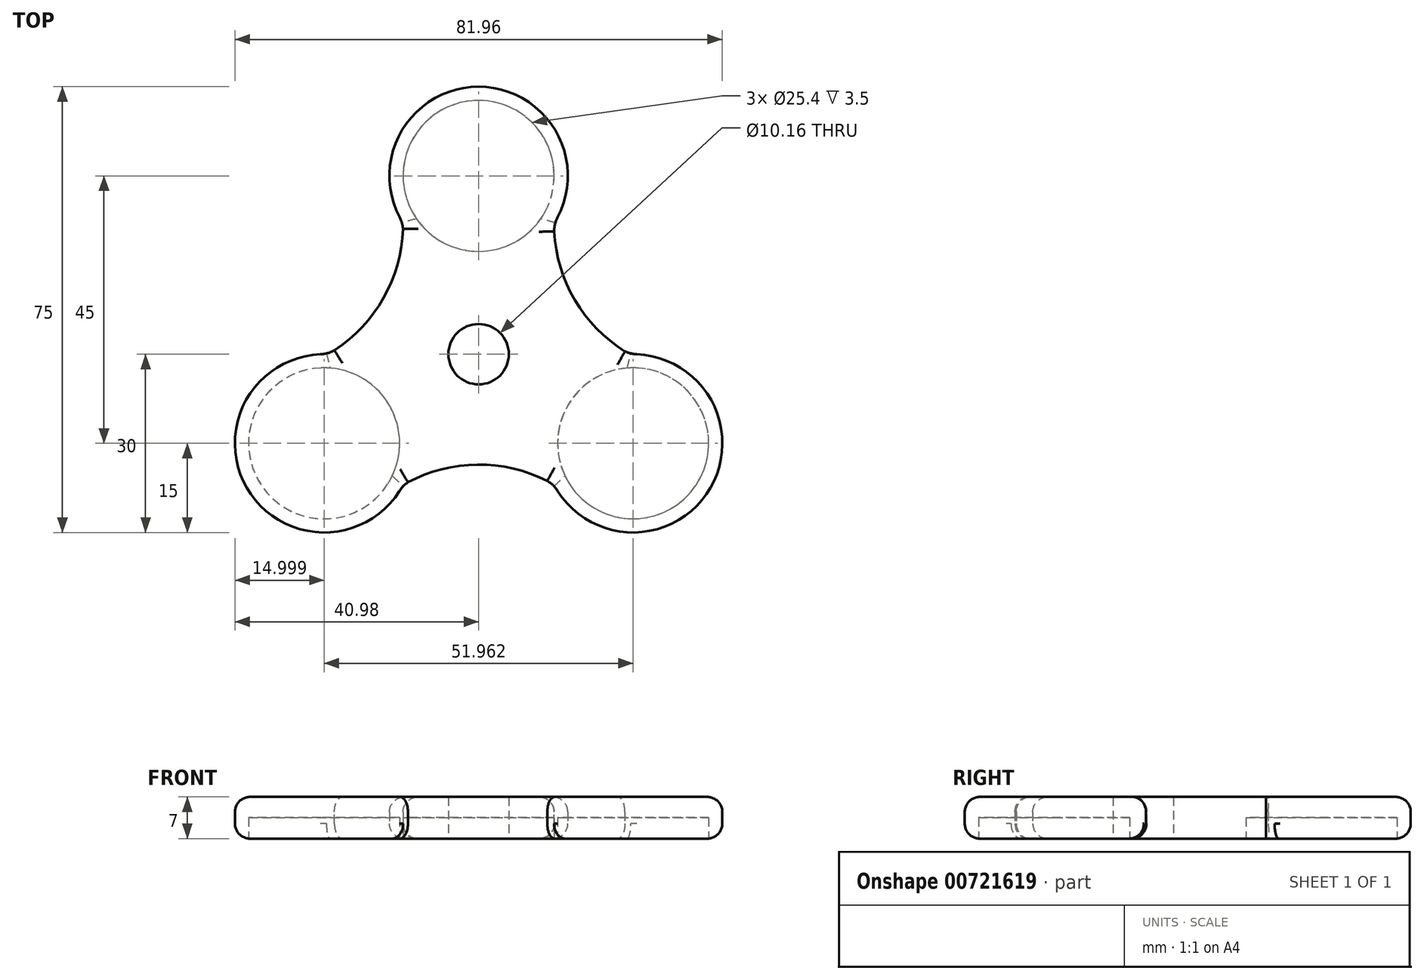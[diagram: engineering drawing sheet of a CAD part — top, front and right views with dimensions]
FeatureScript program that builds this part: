
annotation { "Feature Type Name" : "Feature", "Feature Type Description" : "" }
export const myFeature = defineFeature(function(context is Context, id is Id, definition is map)
    precondition{}
    {
        {
            var Q0;
            Q0=qCreatedBy(makeId("Top.planeOp"),FACE);
            var sketch = newSketch(context, id + "F0", { "sketchPlane" : qUnion([Q0])});
            skCircle(sketch, "E0", {"center": v(0, 0) * mm, "radius": 15 * mm});
            skCircle(sketch, "E1", {"center": v(0, 30) * mm, "radius": 15 * mm});
            skCircle(sketch, "E2", {"center": v(0, 30) * mm, "radius": 12.7 * mm});
            skCircle(sketch, "E3", {"center": v(0, 0) * mm, "radius": 5.08 * mm});
            skLineSegment(sketch, "E4", {"start": v(0, 30) * mm, "end": v(0, 15) * mm, "construction": true});
            skLineSegment(sketch, "E5", {"start": v(0, 0) * mm, "end": v(0, 15) * mm, "construction": true});
            skLineSegment(sketch, "E6", {"start": v(0, 0) * mm, "end": v(0, -15) * mm});
            skLineSegment(sketch, "E7", {"start": v(0, 0) * mm, "end": v(15, 0) * mm});
            skLineSegment(sketch, "E8", {"start": v(0, 0) * mm, "end": v(-15, 0) * mm});
            skLineSegment(sketch, "E9", {"start": v(0, 30) * mm, "end": v(-20.54, 30) * mm, "construction": true});
            skLineSegment(sketch, "E10", {"start": v(-25.98, -15) * mm, "end": v(-25.98, 30.15) * mm, "construction": true});
            skPoint(sketch, "E11", {"position": v(-25.98, 0) * mm});
            skPoint(sketch, "E12", {"position": v(-15, 30) * mm});
            skLineSegment(sketch, "E13.0", {"start": v(12.7, 30) * mm, "end": v(12.7, 15) * mm});
            skLineSegment(sketch, "E13.1", {"start": v(12.7, 0) * mm, "end": v(12.7, 15) * mm});
            skLineSegment(sketch, "E14.0", {"start": v(-12.7, 30) * mm, "end": v(-12.7, 15) * mm});
            skLineSegment(sketch, "E14.1", {"start": v(-12.7, 0) * mm, "end": v(-12.7, 15) * mm});
            skPoint(sketch, "E15.1.0", {"position": v(-18.48, -28) * mm});
            skLineSegment(sketch, "E15.1.1", {"start": v(-19.63, -26) * mm, "end": v(-6.64, -18.5) * mm});
            skLineSegment(sketch, "E15.1.2", {"start": v(-32.33, -4) * mm, "end": v(-19.34, 3.5) * mm});
            skLineSegment(sketch, "E15.1.3", {"start": v(-25.98, -15) * mm, "end": v(-15.71, -32.78) * mm, "construction": true});
            skLineSegment(sketch, "E15.1.4", {"start": v(-25.98, -15) * mm, "end": v(-13, -7.5) * mm, "construction": true});
            skCircle(sketch, "E15.1.5", {"center": v(-25.98, -15) * mm, "radius": 12.7 * mm});
            skCircle(sketch, "E15.1.6", {"center": v(-25.98, -15) * mm, "radius": 15 * mm});
            skLineSegment(sketch, "E15.1.7", {"start": v(6.35, -11) * mm, "end": v(-6.64, -18.5) * mm});
            skLineSegment(sketch, "E15.1.8", {"start": v(-6.35, 11) * mm, "end": v(-19.34, 3.5) * mm});
            skLineSegment(sketch, "E15.1.9", {"start": v(0, 0) * mm, "end": v(-13, -7.5) * mm, "construction": true});
            skPoint(sketch, "E15.2.0", {"position": v(33.48, -2) * mm});
            skLineSegment(sketch, "E15.2.1", {"start": v(32.33, -4) * mm, "end": v(19.34, 3.5) * mm});
            skLineSegment(sketch, "E15.2.2", {"start": v(19.63, -26) * mm, "end": v(6.64, -18.5) * mm});
            skLineSegment(sketch, "E15.2.3", {"start": v(25.98, -15) * mm, "end": v(36.25, 2.78) * mm, "construction": true});
            skLineSegment(sketch, "E15.2.4", {"start": v(25.98, -15) * mm, "end": v(13, -7.5) * mm, "construction": true});
            skCircle(sketch, "E15.2.5", {"center": v(25.98, -15) * mm, "radius": 12.7 * mm});
            skCircle(sketch, "E15.2.6", {"center": v(25.98, -15) * mm, "radius": 15 * mm});
            skLineSegment(sketch, "E15.2.7", {"start": v(6.35, 11) * mm, "end": v(19.34, 3.5) * mm});
            skLineSegment(sketch, "E15.2.8", {"start": v(-6.35, -11) * mm, "end": v(6.64, -18.5) * mm});
            skLineSegment(sketch, "E15.2.9", {"start": v(0, 0) * mm, "end": v(13, -7.5) * mm, "construction": true});
            skSolve(sketch);
        }
        {
            var Q0;
            {var subQ0=sQuery(id+"F0.wireOp",EDGE,"E14.0");var subQ1=sQuery(id+"F0.wireOp",EDGE,"E1");var subQ2=makeQuery(id+"F0.imprint","INTERSECT",VERTEX,{"derivedFrom":[subQ1,subQ0]});Q0=makeQuery(id+"F0.imprint","IMPRINT",FACE,{"disambiguationData":[TD([[makeQuery(id+"F0.imprint","IMPRINT",EDGE,{"disambiguationData":[TD([[subQ2,1.0]])],"derivedFrom":subQ1}),1.0]])]});}
            var Q1;
            {var subQ0=sQuery(id+"F0.wireOp",EDGE,"E13.1");var subQ1=sQuery(id+"F0.wireOp",EDGE,"E0");var subQ2=makeQuery(id+"F0.imprint","INTERSECT",VERTEX,{"derivedFrom":[subQ1,subQ0]});Q1=makeQuery(id+"F0.imprint","IMPRINT",FACE,{"disambiguationData":[TD([[makeQuery(id+"F0.imprint","IMPRINT",EDGE,{"disambiguationData":[TD([[subQ2,-1.0]])],"derivedFrom":subQ1}),-1.0]])]});}
            var Q2;
            {var subQ0=sQuery(id+"F0.wireOp",EDGE,"E14.1");var subQ1=sQuery(id+"F0.wireOp",EDGE,"E0");var subQ2=makeQuery(id+"F0.imprint","INTERSECT",VERTEX,{"derivedFrom":[subQ1,subQ0]});Q2=makeQuery(id+"F0.imprint","IMPRINT",FACE,{"disambiguationData":[TD([[makeQuery(id+"F0.imprint","IMPRINT",EDGE,{"disambiguationData":[TD([[subQ2,1.0]])],"derivedFrom":subQ1}),-1.0]])]});}
            var Q3;
            {var subQ1=sQuery(id+"F0.wireOp",EDGE,"E1");var subQ5=sQuery(id+"F0.wireOp",EDGE,"E14.0");var subQ8=makeQuery(id+"F0.imprint","INTERSECT",VERTEX,{"derivedFrom":[subQ1,subQ5]});Q3=makeQuery(id+"F0.imprint","IMPRINT",FACE,{"disambiguationData":[TD([[makeQuery(id+"F0.imprint","IMPRINT",EDGE,{"disambiguationData":[TD([[subQ8,-1.0]])],"derivedFrom":subQ1}),1.0]])]});}
            var Q4;
            {var subQ0=sQuery(id+"F0.wireOp",EDGE,"E13.1");var subQ5=sQuery(id+"F0.wireOp",EDGE,"E0");var subQ6=makeQuery(id+"F0.imprint","INTERSECT",VERTEX,{"derivedFrom":[subQ5,subQ0]});Q4=makeQuery(id+"F0.imprint","IMPRINT",FACE,{"disambiguationData":[TD([[makeQuery(id+"F0.imprint","IMPRINT",EDGE,{"disambiguationData":[TD([[subQ6,-1.0]])],"derivedFrom":subQ5}),1.0]])]});}
            var Q5;
            {var subQ0=sQuery(id+"F0.wireOp",EDGE,"E7");var subQ1=sQuery(id+"F0.wireOp",EDGE,"E0");var subQ2=makeQuery(id+"F0.imprint","INTERSECT",VERTEX,{"derivedFrom":[subQ1,subQ0]});Q5=makeQuery(id+"F0.imprint","IMPRINT",FACE,{"disambiguationData":[TD([[makeQuery(id+"F0.imprint","IMPRINT",EDGE,{"disambiguationData":[TD([[subQ2,-1.0]])],"derivedFrom":subQ1}),1.0]])]});}
            var Q6;
            {var subQ3=sQuery(id+"F0.wireOp",EDGE,"E0");var subQ7=makeQuery(id+"F0.imprint","INTERSECT",VERTEX,{"derivedFrom":[subQ3,sQuery(id+"F0.wireOp",EDGE,"E7")]});Q6=makeQuery(id+"F0.imprint","IMPRINT",FACE,{"disambiguationData":[TD([[makeQuery(id+"F0.imprint","IMPRINT",EDGE,{"disambiguationData":[TD([[subQ7,-1.0]])],"derivedFrom":subQ3}),-1.0]])]});}
            var Q7;
            {var subQ0=sQuery(id+"F0.wireOp",EDGE,"E15.2.6");var subQ1=sQuery(id+"F0.wireOp",EDGE,"E15.2.1");var subQ2=makeQuery(id+"F0.imprint","INTERSECT",VERTEX,{"derivedFrom":[subQ1,subQ0]});Q7=makeQuery(id+"F0.imprint","IMPRINT",FACE,{"disambiguationData":[TD([[makeQuery(id+"F0.imprint","IMPRINT",EDGE,{"disambiguationData":[TD([[subQ2,1.0]])],"derivedFrom":subQ1}),1.0]])]});}
            var Q8;
            {var subQ0=sQuery(id+"F0.wireOp",EDGE,"E15.2.6");var subQ1=sQuery(id+"F0.wireOp",EDGE,"E15.2.1");var subQ2=makeQuery(id+"F0.imprint","INTERSECT",VERTEX,{"derivedFrom":[subQ1,subQ0]});Q8=makeQuery(id+"F0.imprint","IMPRINT",FACE,{"disambiguationData":[TD([[makeQuery(id+"F0.imprint","IMPRINT",EDGE,{"disambiguationData":[TD([[subQ2,1.0]])],"derivedFrom":subQ1}),-1.0]])]});}
            var Q9;
            {var subQ0=sQuery(id+"F0.wireOp",EDGE,"E15.2.8");var subQ1=sQuery(id+"F0.wireOp",EDGE,"E0");var subQ2=makeQuery(id+"F0.imprint","INTERSECT",VERTEX,{"derivedFrom":[subQ1,subQ0]});Q9=makeQuery(id+"F0.imprint","IMPRINT",FACE,{"disambiguationData":[TD([[makeQuery(id+"F0.imprint","IMPRINT",EDGE,{"disambiguationData":[TD([[subQ2,-1.0]])],"derivedFrom":subQ1}),-1.0]])]});}
            var Q10;
            {var subQ5=sQuery(id+"F0.wireOp",EDGE,"E15.2.8");var subQ6=sQuery(id+"F0.wireOp",EDGE,"E0");var subQ7=makeQuery(id+"F0.imprint","INTERSECT",VERTEX,{"derivedFrom":[subQ6,subQ5]});Q10=makeQuery(id+"F0.imprint","IMPRINT",FACE,{"disambiguationData":[TD([[makeQuery(id+"F0.imprint","IMPRINT",EDGE,{"disambiguationData":[TD([[subQ7,-1.0]])],"derivedFrom":subQ6}),1.0]])]});}
            var Q11;
            {var subQ0=sQuery(id+"F0.wireOp",EDGE,"E8");var subQ6=sQuery(id+"F0.wireOp",EDGE,"E0");var subQ10=makeQuery(id+"F0.imprint","INTERSECT",VERTEX,{"derivedFrom":[subQ6,subQ0]});Q11=makeQuery(id+"F0.imprint","IMPRINT",FACE,{"disambiguationData":[TD([[makeQuery(id+"F0.imprint","IMPRINT",EDGE,{"disambiguationData":[TD([[subQ10,-1.0]])],"derivedFrom":subQ6}),1.0]])]});}
            var Q12;
            {var subQ0=sQuery(id+"F0.wireOp",EDGE,"E8");var subQ1=sQuery(id+"F0.wireOp",EDGE,"E0");var subQ2=makeQuery(id+"F0.imprint","INTERSECT",VERTEX,{"derivedFrom":[subQ1,subQ0]});Q12=makeQuery(id+"F0.imprint","IMPRINT",FACE,{"disambiguationData":[TD([[makeQuery(id+"F0.imprint","IMPRINT",EDGE,{"disambiguationData":[TD([[subQ2,1.0]])],"derivedFrom":subQ1}),1.0]])]});}
            var Q13;
            {var subQ5=sQuery(id+"F0.wireOp",EDGE,"E0");var subQ7=makeQuery(id+"F0.imprint","INTERSECT",VERTEX,{"derivedFrom":[subQ5,sQuery(id+"F0.wireOp",EDGE,"E8")]});Q13=makeQuery(id+"F0.imprint","IMPRINT",FACE,{"disambiguationData":[TD([[makeQuery(id+"F0.imprint","IMPRINT",EDGE,{"disambiguationData":[TD([[subQ7,1.0]])],"derivedFrom":subQ5}),-1.0]])]});}
            var Q14;
            {var subQ0=sQuery(id+"F0.wireOp",EDGE,"E15.1.6");var subQ1=sQuery(id+"F0.wireOp",EDGE,"E15.1.1");var subQ2=makeQuery(id+"F0.imprint","INTERSECT",VERTEX,{"derivedFrom":[subQ1,subQ0]});Q14=makeQuery(id+"F0.imprint","IMPRINT",FACE,{"disambiguationData":[TD([[makeQuery(id+"F0.imprint","IMPRINT",EDGE,{"disambiguationData":[TD([[subQ2,1.0]])],"derivedFrom":subQ1}),1.0]])]});}
            var Q15;
            {var subQ0=sQuery(id+"F0.wireOp",EDGE,"E15.1.6");var subQ1=sQuery(id+"F0.wireOp",EDGE,"E15.1.1");var subQ2=makeQuery(id+"F0.imprint","INTERSECT",VERTEX,{"derivedFrom":[subQ1,subQ0]});Q15=makeQuery(id+"F0.imprint","IMPRINT",FACE,{"disambiguationData":[TD([[makeQuery(id+"F0.imprint","IMPRINT",EDGE,{"disambiguationData":[TD([[subQ2,1.0]])],"derivedFrom":subQ1}),-1.0]])]});}
            var Q16;
            Q16=makeQuery(id+"F0.imprint","IMPRINT",FACE,{"disambiguationData":[TD([[makeQuery(id+"F0.imprint","IMPRINT",EDGE,{"derivedFrom":sQuery(id+"F0.wireOp",EDGE,"E15.1.5")}),-1.0]])]});
            var Q17;
            Q17=makeQuery(id+"F0.imprint","IMPRINT",FACE,{"disambiguationData":[TD([[makeQuery(id+"F0.imprint","IMPRINT",EDGE,{"derivedFrom":sQuery(id+"F0.wireOp",EDGE,"E15.2.5")}),-1.0]])]});
            var Q18;
            {var subQ0=sQuery(id+"F0.wireOp",EDGE,"E15.1.7");var subQ1=sQuery(id+"F0.wireOp",EDGE,"E0");var subQ2=makeQuery(id+"F0.imprint","INTERSECT",VERTEX,{"derivedFrom":[subQ1,subQ0]});Q18=makeQuery(id+"F0.imprint","IMPRINT",FACE,{"disambiguationData":[TD([[makeQuery(id+"F0.imprint","IMPRINT",EDGE,{"disambiguationData":[TD([[subQ2,1.0]])],"derivedFrom":subQ1}),-1.0]])]});}
            extrude(context, id + "F1", {"entities" : qUnion([Q0, Q1, Q2, Q3, Q4, Q5, Q6, Q7, Q8, Q9, Q10, Q11, Q12, Q13, Q14, Q15, Q16, Q17, Q18]), "depth" : 7 * mm, "offsetDistance" : 25.4 * mm, "symmetric" : true});
        }
        {
            var Q0;
            Q0=makeQuery(id+"F1.opExtrude","SWEPT_EDGE",EDGE,{"disambiguationData":[OSD([sQuery(id+"F0.wireOp",EDGE,"E1"),sQuery(id+"F0.wireOp",EDGE,"E14.0")])]});
            var Q1;
            Q1=makeQuery(id+"F1.opExtrude","SWEPT_EDGE",EDGE,{"disambiguationData":[OSD([sQuery(id+"F0.wireOp",EDGE,"E15.1.2"),sQuery(id+"F0.wireOp",EDGE,"E15.1.6")])]});
            var Q2;
            Q2=makeQuery(id+"F1.opExtrude","SWEPT_EDGE",EDGE,{"disambiguationData":[OSD([sQuery(id+"F0.wireOp",EDGE,"E15.1.1"),sQuery(id+"F0.wireOp",EDGE,"E15.1.6")])]});
            var Q3;
            Q3=makeQuery(id+"F1.opExtrude","SWEPT_EDGE",EDGE,{"disambiguationData":[OSD([sQuery(id+"F0.wireOp",EDGE,"E15.2.2"),sQuery(id+"F0.wireOp",EDGE,"E15.2.6")])]});
            var Q4;
            Q4=makeQuery(id+"F1.opExtrude","SWEPT_EDGE",EDGE,{"disambiguationData":[OSD([sQuery(id+"F0.wireOp",EDGE,"E15.2.1"),sQuery(id+"F0.wireOp",EDGE,"E15.2.6")])]});
            var Q5;
            Q5=makeQuery(id+"F1.opExtrude","SWEPT_EDGE",EDGE,{"disambiguationData":[OSD([sQuery(id+"F0.wireOp",EDGE,"E1"),sQuery(id+"F0.wireOp",EDGE,"E13.0")])]});
            fillet(context, id + "F2", {"entities" : qUnion([Q0, Q1, Q2, Q3, Q4, Q5]), "radius" : 5.08 * mm, "tangentPropagation" : true, "allowEdgeOverflow" : false});
        }
        {
            var Q0;
            Q0=makeQuery(id+"F1.opExtrude","SWEPT_EDGE",EDGE,{"disambiguationData":[OSD([sQuery(id+"F0.wireOp",EDGE,"E13.1"),sQuery(id+"F0.wireOp",EDGE,"E15.2.7")])]});
            var Q1;
            Q1=makeQuery(id+"F1.opExtrude","SWEPT_EDGE",EDGE,{"disambiguationData":[OSD([sQuery(id+"F0.wireOp",EDGE,"E14.1"),sQuery(id+"F0.wireOp",EDGE,"E15.1.8")])]});
            var Q2;
            Q2=makeQuery(id+"F1.opExtrude","SWEPT_EDGE",EDGE,{"disambiguationData":[OSD([sQuery(id+"F0.wireOp",EDGE,"E6"),sQuery(id+"F0.wireOp",EDGE,"E15.1.7"),sQuery(id+"F0.wireOp",EDGE,"E15.2.8")])]});
            fillet(context, id + "F3", {"entities" : qUnion([Q0, Q1, Q2]), "radius" : 25.4 * mm, "tangentPropagation" : true, "allowEdgeOverflow" : false});
        }
        {
            var Q0;
            {var subQ0=sQuery(id+"F0.wireOp",EDGE,"E2");var subQ1=makeQuery(id+"F0.imprint","INTERSECT",VERTEX,{"derivedFrom":[subQ0,sQuery(id+"F0.wireOp",EDGE,"E13.0")]});Q0=makeQuery(id+"F0.imprint","IMPRINT",FACE,{"disambiguationData":[TD([[makeQuery(id+"F0.imprint","IMPRINT",EDGE,{"disambiguationData":[TD([[subQ1,1.0]])],"derivedFrom":subQ0}),1.0]])]});}
            var Q1;
            {var subQ0=sQuery(id+"F0.wireOp",EDGE,"E15.2.5");var subQ1=makeQuery(id+"F0.imprint","INTERSECT",VERTEX,{"derivedFrom":[sQuery(id+"F0.wireOp",EDGE,"E15.2.1"),subQ0]});Q1=makeQuery(id+"F0.imprint","IMPRINT",FACE,{"disambiguationData":[TD([[makeQuery(id+"F0.imprint","IMPRINT",EDGE,{"disambiguationData":[TD([[subQ1,-1.0]])],"derivedFrom":subQ0}),1.0]])]});}
            var Q2;
            {var subQ0=sQuery(id+"F0.wireOp",EDGE,"E15.1.5");var subQ1=makeQuery(id+"F0.imprint","INTERSECT",VERTEX,{"derivedFrom":[sQuery(id+"F0.wireOp",EDGE,"E15.1.1"),subQ0]});Q2=makeQuery(id+"F0.imprint","IMPRINT",FACE,{"disambiguationData":[TD([[makeQuery(id+"F0.imprint","IMPRINT",EDGE,{"disambiguationData":[TD([[subQ1,-1.0]])],"derivedFrom":subQ0}),1.0]])]});}
            var Q3;
            Q3=makeQuery(id+"F1.opExtrude","CAP_FACE",FACE,{"disambiguationData":[OSD([sQuery(id+"F0.wireOp",EDGE,"E1"),sQuery(id+"F0.wireOp",EDGE,"E2"),sQuery(id+"F0.wireOp",EDGE,"E3"),sQuery(id+"F0.wireOp",EDGE,"E13.0"),sQuery(id+"F0.wireOp",EDGE,"E13.1"),sQuery(id+"F0.wireOp",EDGE,"E14.0"),sQuery(id+"F0.wireOp",EDGE,"E14.1"),sQuery(id+"F0.wireOp",EDGE,"E15.1.1"),sQuery(id+"F0.wireOp",EDGE,"E15.1.2"),sQuery(id+"F0.wireOp",EDGE,"E15.1.5"),sQuery(id+"F0.wireOp",EDGE,"E15.1.6"),sQuery(id+"F0.wireOp",EDGE,"E15.1.7"),sQuery(id+"F0.wireOp",EDGE,"E15.1.8"),sQuery(id+"F0.wireOp",EDGE,"E15.2.1"),sQuery(id+"F0.wireOp",EDGE,"E15.2.2"),sQuery(id+"F0.wireOp",EDGE,"E15.2.5"),sQuery(id+"F0.wireOp",EDGE,"E15.2.6"),sQuery(id+"F0.wireOp",EDGE,"E15.2.7"),sQuery(id+"F0.wireOp",EDGE,"E15.2.8")])],"isStart":false});
            extrude(context, id + "F4", {"entities" : qUnion([Q0, Q1, Q2]), "operationType" : NewBodyOperationType.ADD, "endBound" : BoundingType.UP_TO_SURFACE, "depth" : 25.4 * mm, "endBoundEntityFace" : qUnion([Q3]), "offsetDistance" : 25.4 * mm});
        }
        {
            var Q0;
            {var subQ0=sQuery(id+"F0.wireOp",EDGE,"E15.2.8");var subQ1=sQuery(id+"F0.wireOp",EDGE,"E15.1.7");Q0=makeQuery(id+"F3.opFillet","BLEND_EDGE",EDGE,{"blendedFrom":[makeQuery(id+"F1.opExtrude","SWEPT_EDGE",EDGE,{"disambiguationData":[OSD([sQuery(id+"F0.wireOp",EDGE,"E6"),subQ1,subQ0])]}),makeQuery(id+"F1.opExtrude","CAP_FACE",FACE,{"disambiguationData":[OSD([sQuery(id+"F0.wireOp",EDGE,"E1"),sQuery(id+"F0.wireOp",EDGE,"E2"),sQuery(id+"F0.wireOp",EDGE,"E3"),sQuery(id+"F0.wireOp",EDGE,"E13.0"),sQuery(id+"F0.wireOp",EDGE,"E13.1"),sQuery(id+"F0.wireOp",EDGE,"E14.0"),sQuery(id+"F0.wireOp",EDGE,"E14.1"),sQuery(id+"F0.wireOp",EDGE,"E15.1.1"),sQuery(id+"F0.wireOp",EDGE,"E15.1.2"),sQuery(id+"F0.wireOp",EDGE,"E15.1.5"),sQuery(id+"F0.wireOp",EDGE,"E15.1.6"),subQ1,sQuery(id+"F0.wireOp",EDGE,"E15.1.8"),sQuery(id+"F0.wireOp",EDGE,"E15.2.1"),sQuery(id+"F0.wireOp",EDGE,"E15.2.2"),sQuery(id+"F0.wireOp",EDGE,"E15.2.5"),sQuery(id+"F0.wireOp",EDGE,"E15.2.6"),sQuery(id+"F0.wireOp",EDGE,"E15.2.7"),subQ0])],"isStart":false})],"blendedInto":[makeQuery(id+"F1.opExtrude","CAP_FACE",FACE,{"disambiguationData":[OSD([sQuery(id+"F0.wireOp",EDGE,"E1"),sQuery(id+"F0.wireOp",EDGE,"E2"),sQuery(id+"F0.wireOp",EDGE,"E3"),sQuery(id+"F0.wireOp",EDGE,"E13.0"),sQuery(id+"F0.wireOp",EDGE,"E13.1"),sQuery(id+"F0.wireOp",EDGE,"E14.0"),sQuery(id+"F0.wireOp",EDGE,"E14.1"),sQuery(id+"F0.wireOp",EDGE,"E15.1.1"),sQuery(id+"F0.wireOp",EDGE,"E15.1.2"),sQuery(id+"F0.wireOp",EDGE,"E15.1.5"),sQuery(id+"F0.wireOp",EDGE,"E15.1.6"),subQ1,sQuery(id+"F0.wireOp",EDGE,"E15.1.8"),sQuery(id+"F0.wireOp",EDGE,"E15.2.1"),sQuery(id+"F0.wireOp",EDGE,"E15.2.2"),sQuery(id+"F0.wireOp",EDGE,"E15.2.5"),sQuery(id+"F0.wireOp",EDGE,"E15.2.6"),sQuery(id+"F0.wireOp",EDGE,"E15.2.7"),subQ0])],"isStart":false})]});}
            var Q1;
            {var subQ0=sQuery(id+"F0.wireOp",EDGE,"E15.1.6");var subQ1=sQuery(id+"F0.wireOp",EDGE,"E15.1.1");Q1=makeQuery(id+"F2.opFillet","BLEND_EDGE",EDGE,{"blendedFrom":[makeQuery(id+"F1.opExtrude","SWEPT_EDGE",EDGE,{"disambiguationData":[OSD([subQ1,subQ0])]}),makeQuery(id+"F1.opExtrude","CAP_FACE",FACE,{"disambiguationData":[OSD([sQuery(id+"F0.wireOp",EDGE,"E1"),sQuery(id+"F0.wireOp",EDGE,"E2"),sQuery(id+"F0.wireOp",EDGE,"E3"),sQuery(id+"F0.wireOp",EDGE,"E13.0"),sQuery(id+"F0.wireOp",EDGE,"E13.1"),sQuery(id+"F0.wireOp",EDGE,"E14.0"),sQuery(id+"F0.wireOp",EDGE,"E14.1"),subQ1,sQuery(id+"F0.wireOp",EDGE,"E15.1.2"),sQuery(id+"F0.wireOp",EDGE,"E15.1.5"),subQ0,sQuery(id+"F0.wireOp",EDGE,"E15.1.7"),sQuery(id+"F0.wireOp",EDGE,"E15.1.8"),sQuery(id+"F0.wireOp",EDGE,"E15.2.1"),sQuery(id+"F0.wireOp",EDGE,"E15.2.2"),sQuery(id+"F0.wireOp",EDGE,"E15.2.5"),sQuery(id+"F0.wireOp",EDGE,"E15.2.6"),sQuery(id+"F0.wireOp",EDGE,"E15.2.7"),sQuery(id+"F0.wireOp",EDGE,"E15.2.8")])],"isStart":false})],"blendedInto":[makeQuery(id+"F1.opExtrude","CAP_FACE",FACE,{"disambiguationData":[OSD([sQuery(id+"F0.wireOp",EDGE,"E1"),sQuery(id+"F0.wireOp",EDGE,"E2"),sQuery(id+"F0.wireOp",EDGE,"E3"),sQuery(id+"F0.wireOp",EDGE,"E13.0"),sQuery(id+"F0.wireOp",EDGE,"E13.1"),sQuery(id+"F0.wireOp",EDGE,"E14.0"),sQuery(id+"F0.wireOp",EDGE,"E14.1"),subQ1,sQuery(id+"F0.wireOp",EDGE,"E15.1.2"),sQuery(id+"F0.wireOp",EDGE,"E15.1.5"),subQ0,sQuery(id+"F0.wireOp",EDGE,"E15.1.7"),sQuery(id+"F0.wireOp",EDGE,"E15.1.8"),sQuery(id+"F0.wireOp",EDGE,"E15.2.1"),sQuery(id+"F0.wireOp",EDGE,"E15.2.2"),sQuery(id+"F0.wireOp",EDGE,"E15.2.5"),sQuery(id+"F0.wireOp",EDGE,"E15.2.6"),sQuery(id+"F0.wireOp",EDGE,"E15.2.7"),sQuery(id+"F0.wireOp",EDGE,"E15.2.8")])],"isStart":false})]});}
            var Q2;
            Q2=makeQuery(id+"F1.opExtrude","CAP_EDGE",EDGE,{"disambiguationData":[OSD([sQuery(id+"F0.wireOp",EDGE,"E15.1.6")])],"isStart":false});
            var Q3;
            {var subQ0=sQuery(id+"F0.wireOp",EDGE,"E15.2.6");var subQ1=sQuery(id+"F0.wireOp",EDGE,"E15.2.2");Q3=makeQuery(id+"F2.opFillet","BLEND_EDGE",EDGE,{"blendedFrom":[makeQuery(id+"F1.opExtrude","SWEPT_EDGE",EDGE,{"disambiguationData":[OSD([subQ1,subQ0])]}),makeQuery(id+"F1.opExtrude","CAP_FACE",FACE,{"disambiguationData":[OSD([sQuery(id+"F0.wireOp",EDGE,"E1"),sQuery(id+"F0.wireOp",EDGE,"E2"),sQuery(id+"F0.wireOp",EDGE,"E3"),sQuery(id+"F0.wireOp",EDGE,"E13.0"),sQuery(id+"F0.wireOp",EDGE,"E13.1"),sQuery(id+"F0.wireOp",EDGE,"E14.0"),sQuery(id+"F0.wireOp",EDGE,"E14.1"),sQuery(id+"F0.wireOp",EDGE,"E15.1.1"),sQuery(id+"F0.wireOp",EDGE,"E15.1.2"),sQuery(id+"F0.wireOp",EDGE,"E15.1.5"),sQuery(id+"F0.wireOp",EDGE,"E15.1.6"),sQuery(id+"F0.wireOp",EDGE,"E15.1.7"),sQuery(id+"F0.wireOp",EDGE,"E15.1.8"),sQuery(id+"F0.wireOp",EDGE,"E15.2.1"),subQ1,sQuery(id+"F0.wireOp",EDGE,"E15.2.5"),subQ0,sQuery(id+"F0.wireOp",EDGE,"E15.2.7"),sQuery(id+"F0.wireOp",EDGE,"E15.2.8")])],"isStart":false})],"blendedInto":[makeQuery(id+"F1.opExtrude","CAP_FACE",FACE,{"disambiguationData":[OSD([sQuery(id+"F0.wireOp",EDGE,"E1"),sQuery(id+"F0.wireOp",EDGE,"E2"),sQuery(id+"F0.wireOp",EDGE,"E3"),sQuery(id+"F0.wireOp",EDGE,"E13.0"),sQuery(id+"F0.wireOp",EDGE,"E13.1"),sQuery(id+"F0.wireOp",EDGE,"E14.0"),sQuery(id+"F0.wireOp",EDGE,"E14.1"),sQuery(id+"F0.wireOp",EDGE,"E15.1.1"),sQuery(id+"F0.wireOp",EDGE,"E15.1.2"),sQuery(id+"F0.wireOp",EDGE,"E15.1.5"),sQuery(id+"F0.wireOp",EDGE,"E15.1.6"),sQuery(id+"F0.wireOp",EDGE,"E15.1.7"),sQuery(id+"F0.wireOp",EDGE,"E15.1.8"),sQuery(id+"F0.wireOp",EDGE,"E15.2.1"),subQ1,sQuery(id+"F0.wireOp",EDGE,"E15.2.5"),subQ0,sQuery(id+"F0.wireOp",EDGE,"E15.2.7"),sQuery(id+"F0.wireOp",EDGE,"E15.2.8")])],"isStart":false})]});}
            var Q4;
            Q4=makeQuery(id+"F1.opExtrude","CAP_EDGE",EDGE,{"disambiguationData":[OSD([sQuery(id+"F0.wireOp",EDGE,"E15.2.6")])],"isStart":false});
            var Q5;
            {var subQ0=sQuery(id+"F0.wireOp",EDGE,"E15.2.7");var subQ1=sQuery(id+"F0.wireOp",EDGE,"E13.1");Q5=makeQuery(id+"F3.opFillet","BLEND_EDGE",EDGE,{"blendedFrom":[makeQuery(id+"F1.opExtrude","SWEPT_EDGE",EDGE,{"disambiguationData":[OSD([subQ1,subQ0])]}),makeQuery(id+"F1.opExtrude","CAP_FACE",FACE,{"disambiguationData":[OSD([sQuery(id+"F0.wireOp",EDGE,"E1"),sQuery(id+"F0.wireOp",EDGE,"E2"),sQuery(id+"F0.wireOp",EDGE,"E3"),sQuery(id+"F0.wireOp",EDGE,"E13.0"),subQ1,sQuery(id+"F0.wireOp",EDGE,"E14.0"),sQuery(id+"F0.wireOp",EDGE,"E14.1"),sQuery(id+"F0.wireOp",EDGE,"E15.1.1"),sQuery(id+"F0.wireOp",EDGE,"E15.1.2"),sQuery(id+"F0.wireOp",EDGE,"E15.1.5"),sQuery(id+"F0.wireOp",EDGE,"E15.1.6"),sQuery(id+"F0.wireOp",EDGE,"E15.1.7"),sQuery(id+"F0.wireOp",EDGE,"E15.1.8"),sQuery(id+"F0.wireOp",EDGE,"E15.2.1"),sQuery(id+"F0.wireOp",EDGE,"E15.2.2"),sQuery(id+"F0.wireOp",EDGE,"E15.2.5"),sQuery(id+"F0.wireOp",EDGE,"E15.2.6"),subQ0,sQuery(id+"F0.wireOp",EDGE,"E15.2.8")])],"isStart":false})],"blendedInto":[makeQuery(id+"F1.opExtrude","CAP_FACE",FACE,{"disambiguationData":[OSD([sQuery(id+"F0.wireOp",EDGE,"E1"),sQuery(id+"F0.wireOp",EDGE,"E2"),sQuery(id+"F0.wireOp",EDGE,"E3"),sQuery(id+"F0.wireOp",EDGE,"E13.0"),subQ1,sQuery(id+"F0.wireOp",EDGE,"E14.0"),sQuery(id+"F0.wireOp",EDGE,"E14.1"),sQuery(id+"F0.wireOp",EDGE,"E15.1.1"),sQuery(id+"F0.wireOp",EDGE,"E15.1.2"),sQuery(id+"F0.wireOp",EDGE,"E15.1.5"),sQuery(id+"F0.wireOp",EDGE,"E15.1.6"),sQuery(id+"F0.wireOp",EDGE,"E15.1.7"),sQuery(id+"F0.wireOp",EDGE,"E15.1.8"),sQuery(id+"F0.wireOp",EDGE,"E15.2.1"),sQuery(id+"F0.wireOp",EDGE,"E15.2.2"),sQuery(id+"F0.wireOp",EDGE,"E15.2.5"),sQuery(id+"F0.wireOp",EDGE,"E15.2.6"),subQ0,sQuery(id+"F0.wireOp",EDGE,"E15.2.8")])],"isStart":false})]});}
            var Q6;
            {var subQ0=sQuery(id+"F0.wireOp",EDGE,"E15.2.6");var subQ1=sQuery(id+"F0.wireOp",EDGE,"E15.2.1");Q6=makeQuery(id+"F2.opFillet","BLEND_EDGE",EDGE,{"blendedFrom":[makeQuery(id+"F1.opExtrude","SWEPT_EDGE",EDGE,{"disambiguationData":[OSD([subQ1,subQ0])]}),makeQuery(id+"F1.opExtrude","CAP_FACE",FACE,{"disambiguationData":[OSD([sQuery(id+"F0.wireOp",EDGE,"E1"),sQuery(id+"F0.wireOp",EDGE,"E2"),sQuery(id+"F0.wireOp",EDGE,"E3"),sQuery(id+"F0.wireOp",EDGE,"E13.0"),sQuery(id+"F0.wireOp",EDGE,"E13.1"),sQuery(id+"F0.wireOp",EDGE,"E14.0"),sQuery(id+"F0.wireOp",EDGE,"E14.1"),sQuery(id+"F0.wireOp",EDGE,"E15.1.1"),sQuery(id+"F0.wireOp",EDGE,"E15.1.2"),sQuery(id+"F0.wireOp",EDGE,"E15.1.5"),sQuery(id+"F0.wireOp",EDGE,"E15.1.6"),sQuery(id+"F0.wireOp",EDGE,"E15.1.7"),sQuery(id+"F0.wireOp",EDGE,"E15.1.8"),subQ1,sQuery(id+"F0.wireOp",EDGE,"E15.2.2"),sQuery(id+"F0.wireOp",EDGE,"E15.2.5"),subQ0,sQuery(id+"F0.wireOp",EDGE,"E15.2.7"),sQuery(id+"F0.wireOp",EDGE,"E15.2.8")])],"isStart":false})],"blendedInto":[makeQuery(id+"F1.opExtrude","CAP_FACE",FACE,{"disambiguationData":[OSD([sQuery(id+"F0.wireOp",EDGE,"E1"),sQuery(id+"F0.wireOp",EDGE,"E2"),sQuery(id+"F0.wireOp",EDGE,"E3"),sQuery(id+"F0.wireOp",EDGE,"E13.0"),sQuery(id+"F0.wireOp",EDGE,"E13.1"),sQuery(id+"F0.wireOp",EDGE,"E14.0"),sQuery(id+"F0.wireOp",EDGE,"E14.1"),sQuery(id+"F0.wireOp",EDGE,"E15.1.1"),sQuery(id+"F0.wireOp",EDGE,"E15.1.2"),sQuery(id+"F0.wireOp",EDGE,"E15.1.5"),sQuery(id+"F0.wireOp",EDGE,"E15.1.6"),sQuery(id+"F0.wireOp",EDGE,"E15.1.7"),sQuery(id+"F0.wireOp",EDGE,"E15.1.8"),subQ1,sQuery(id+"F0.wireOp",EDGE,"E15.2.2"),sQuery(id+"F0.wireOp",EDGE,"E15.2.5"),subQ0,sQuery(id+"F0.wireOp",EDGE,"E15.2.7"),sQuery(id+"F0.wireOp",EDGE,"E15.2.8")])],"isStart":false})]});}
            var Q7;
            {var subQ0=sQuery(id+"F0.wireOp",EDGE,"E13.0");var subQ1=sQuery(id+"F0.wireOp",EDGE,"E1");Q7=makeQuery(id+"F2.opFillet","BLEND_EDGE",EDGE,{"blendedFrom":[makeQuery(id+"F1.opExtrude","SWEPT_EDGE",EDGE,{"disambiguationData":[OSD([subQ1,subQ0])]}),makeQuery(id+"F1.opExtrude","CAP_FACE",FACE,{"disambiguationData":[OSD([subQ1,sQuery(id+"F0.wireOp",EDGE,"E2"),sQuery(id+"F0.wireOp",EDGE,"E3"),subQ0,sQuery(id+"F0.wireOp",EDGE,"E13.1"),sQuery(id+"F0.wireOp",EDGE,"E14.0"),sQuery(id+"F0.wireOp",EDGE,"E14.1"),sQuery(id+"F0.wireOp",EDGE,"E15.1.1"),sQuery(id+"F0.wireOp",EDGE,"E15.1.2"),sQuery(id+"F0.wireOp",EDGE,"E15.1.5"),sQuery(id+"F0.wireOp",EDGE,"E15.1.6"),sQuery(id+"F0.wireOp",EDGE,"E15.1.7"),sQuery(id+"F0.wireOp",EDGE,"E15.1.8"),sQuery(id+"F0.wireOp",EDGE,"E15.2.1"),sQuery(id+"F0.wireOp",EDGE,"E15.2.2"),sQuery(id+"F0.wireOp",EDGE,"E15.2.5"),sQuery(id+"F0.wireOp",EDGE,"E15.2.6"),sQuery(id+"F0.wireOp",EDGE,"E15.2.7"),sQuery(id+"F0.wireOp",EDGE,"E15.2.8")])],"isStart":false})],"blendedInto":[makeQuery(id+"F1.opExtrude","CAP_FACE",FACE,{"disambiguationData":[OSD([subQ1,sQuery(id+"F0.wireOp",EDGE,"E2"),sQuery(id+"F0.wireOp",EDGE,"E3"),subQ0,sQuery(id+"F0.wireOp",EDGE,"E13.1"),sQuery(id+"F0.wireOp",EDGE,"E14.0"),sQuery(id+"F0.wireOp",EDGE,"E14.1"),sQuery(id+"F0.wireOp",EDGE,"E15.1.1"),sQuery(id+"F0.wireOp",EDGE,"E15.1.2"),sQuery(id+"F0.wireOp",EDGE,"E15.1.5"),sQuery(id+"F0.wireOp",EDGE,"E15.1.6"),sQuery(id+"F0.wireOp",EDGE,"E15.1.7"),sQuery(id+"F0.wireOp",EDGE,"E15.1.8"),sQuery(id+"F0.wireOp",EDGE,"E15.2.1"),sQuery(id+"F0.wireOp",EDGE,"E15.2.2"),sQuery(id+"F0.wireOp",EDGE,"E15.2.5"),sQuery(id+"F0.wireOp",EDGE,"E15.2.6"),sQuery(id+"F0.wireOp",EDGE,"E15.2.7"),sQuery(id+"F0.wireOp",EDGE,"E15.2.8")])],"isStart":false})]});}
            var Q8;
            Q8=makeQuery(id+"F1.opExtrude","CAP_EDGE",EDGE,{"disambiguationData":[OSD([sQuery(id+"F0.wireOp",EDGE,"E1")])],"isStart":false});
            var Q9;
            {var subQ0=sQuery(id+"F0.wireOp",EDGE,"E15.1.8");var subQ1=sQuery(id+"F0.wireOp",EDGE,"E14.1");Q9=makeQuery(id+"F3.opFillet","BLEND_EDGE",EDGE,{"blendedFrom":[makeQuery(id+"F1.opExtrude","SWEPT_EDGE",EDGE,{"disambiguationData":[OSD([subQ1,subQ0])]}),makeQuery(id+"F1.opExtrude","CAP_FACE",FACE,{"disambiguationData":[OSD([sQuery(id+"F0.wireOp",EDGE,"E1"),sQuery(id+"F0.wireOp",EDGE,"E2"),sQuery(id+"F0.wireOp",EDGE,"E3"),sQuery(id+"F0.wireOp",EDGE,"E13.0"),sQuery(id+"F0.wireOp",EDGE,"E13.1"),sQuery(id+"F0.wireOp",EDGE,"E14.0"),subQ1,sQuery(id+"F0.wireOp",EDGE,"E15.1.1"),sQuery(id+"F0.wireOp",EDGE,"E15.1.2"),sQuery(id+"F0.wireOp",EDGE,"E15.1.5"),sQuery(id+"F0.wireOp",EDGE,"E15.1.6"),sQuery(id+"F0.wireOp",EDGE,"E15.1.7"),subQ0,sQuery(id+"F0.wireOp",EDGE,"E15.2.1"),sQuery(id+"F0.wireOp",EDGE,"E15.2.2"),sQuery(id+"F0.wireOp",EDGE,"E15.2.5"),sQuery(id+"F0.wireOp",EDGE,"E15.2.6"),sQuery(id+"F0.wireOp",EDGE,"E15.2.7"),sQuery(id+"F0.wireOp",EDGE,"E15.2.8")])],"isStart":false})],"blendedInto":[makeQuery(id+"F1.opExtrude","CAP_FACE",FACE,{"disambiguationData":[OSD([sQuery(id+"F0.wireOp",EDGE,"E1"),sQuery(id+"F0.wireOp",EDGE,"E2"),sQuery(id+"F0.wireOp",EDGE,"E3"),sQuery(id+"F0.wireOp",EDGE,"E13.0"),sQuery(id+"F0.wireOp",EDGE,"E13.1"),sQuery(id+"F0.wireOp",EDGE,"E14.0"),subQ1,sQuery(id+"F0.wireOp",EDGE,"E15.1.1"),sQuery(id+"F0.wireOp",EDGE,"E15.1.2"),sQuery(id+"F0.wireOp",EDGE,"E15.1.5"),sQuery(id+"F0.wireOp",EDGE,"E15.1.6"),sQuery(id+"F0.wireOp",EDGE,"E15.1.7"),subQ0,sQuery(id+"F0.wireOp",EDGE,"E15.2.1"),sQuery(id+"F0.wireOp",EDGE,"E15.2.2"),sQuery(id+"F0.wireOp",EDGE,"E15.2.5"),sQuery(id+"F0.wireOp",EDGE,"E15.2.6"),sQuery(id+"F0.wireOp",EDGE,"E15.2.7"),sQuery(id+"F0.wireOp",EDGE,"E15.2.8")])],"isStart":false})]});}
            var Q10;
            {var subQ0=sQuery(id+"F0.wireOp",EDGE,"E14.0");var subQ1=sQuery(id+"F0.wireOp",EDGE,"E1");Q10=makeQuery(id+"F2.opFillet","BLEND_EDGE",EDGE,{"blendedFrom":[makeQuery(id+"F1.opExtrude","SWEPT_EDGE",EDGE,{"disambiguationData":[OSD([subQ1,subQ0])]}),makeQuery(id+"F1.opExtrude","CAP_FACE",FACE,{"disambiguationData":[OSD([subQ1,sQuery(id+"F0.wireOp",EDGE,"E2"),sQuery(id+"F0.wireOp",EDGE,"E3"),sQuery(id+"F0.wireOp",EDGE,"E13.0"),sQuery(id+"F0.wireOp",EDGE,"E13.1"),subQ0,sQuery(id+"F0.wireOp",EDGE,"E14.1"),sQuery(id+"F0.wireOp",EDGE,"E15.1.1"),sQuery(id+"F0.wireOp",EDGE,"E15.1.2"),sQuery(id+"F0.wireOp",EDGE,"E15.1.5"),sQuery(id+"F0.wireOp",EDGE,"E15.1.6"),sQuery(id+"F0.wireOp",EDGE,"E15.1.7"),sQuery(id+"F0.wireOp",EDGE,"E15.1.8"),sQuery(id+"F0.wireOp",EDGE,"E15.2.1"),sQuery(id+"F0.wireOp",EDGE,"E15.2.2"),sQuery(id+"F0.wireOp",EDGE,"E15.2.5"),sQuery(id+"F0.wireOp",EDGE,"E15.2.6"),sQuery(id+"F0.wireOp",EDGE,"E15.2.7"),sQuery(id+"F0.wireOp",EDGE,"E15.2.8")])],"isStart":false})],"blendedInto":[makeQuery(id+"F1.opExtrude","CAP_FACE",FACE,{"disambiguationData":[OSD([subQ1,sQuery(id+"F0.wireOp",EDGE,"E2"),sQuery(id+"F0.wireOp",EDGE,"E3"),sQuery(id+"F0.wireOp",EDGE,"E13.0"),sQuery(id+"F0.wireOp",EDGE,"E13.1"),subQ0,sQuery(id+"F0.wireOp",EDGE,"E14.1"),sQuery(id+"F0.wireOp",EDGE,"E15.1.1"),sQuery(id+"F0.wireOp",EDGE,"E15.1.2"),sQuery(id+"F0.wireOp",EDGE,"E15.1.5"),sQuery(id+"F0.wireOp",EDGE,"E15.1.6"),sQuery(id+"F0.wireOp",EDGE,"E15.1.7"),sQuery(id+"F0.wireOp",EDGE,"E15.1.8"),sQuery(id+"F0.wireOp",EDGE,"E15.2.1"),sQuery(id+"F0.wireOp",EDGE,"E15.2.2"),sQuery(id+"F0.wireOp",EDGE,"E15.2.5"),sQuery(id+"F0.wireOp",EDGE,"E15.2.6"),sQuery(id+"F0.wireOp",EDGE,"E15.2.7"),sQuery(id+"F0.wireOp",EDGE,"E15.2.8")])],"isStart":false})]});}
            var Q11;
            {var subQ0=sQuery(id+"F0.wireOp",EDGE,"E15.1.8");var subQ1=sQuery(id+"F0.wireOp",EDGE,"E14.1");Q11=makeQuery(id+"F3.opFillet","BLEND_EDGE",EDGE,{"blendedFrom":[makeQuery(id+"F1.opExtrude","SWEPT_EDGE",EDGE,{"disambiguationData":[OSD([subQ1,subQ0])]}),makeQuery(id+"F1.opExtrude","CAP_FACE",FACE,{"disambiguationData":[OSD([sQuery(id+"F0.wireOp",EDGE,"E1"),sQuery(id+"F0.wireOp",EDGE,"E2"),sQuery(id+"F0.wireOp",EDGE,"E3"),sQuery(id+"F0.wireOp",EDGE,"E13.0"),sQuery(id+"F0.wireOp",EDGE,"E13.1"),sQuery(id+"F0.wireOp",EDGE,"E14.0"),subQ1,sQuery(id+"F0.wireOp",EDGE,"E15.1.1"),sQuery(id+"F0.wireOp",EDGE,"E15.1.2"),sQuery(id+"F0.wireOp",EDGE,"E15.1.5"),sQuery(id+"F0.wireOp",EDGE,"E15.1.6"),sQuery(id+"F0.wireOp",EDGE,"E15.1.7"),subQ0,sQuery(id+"F0.wireOp",EDGE,"E15.2.1"),sQuery(id+"F0.wireOp",EDGE,"E15.2.2"),sQuery(id+"F0.wireOp",EDGE,"E15.2.5"),sQuery(id+"F0.wireOp",EDGE,"E15.2.6"),sQuery(id+"F0.wireOp",EDGE,"E15.2.7"),sQuery(id+"F0.wireOp",EDGE,"E15.2.8")])],"isStart":true})],"blendedInto":[makeQuery(id+"F1.opExtrude","CAP_FACE",FACE,{"disambiguationData":[OSD([sQuery(id+"F0.wireOp",EDGE,"E1"),sQuery(id+"F0.wireOp",EDGE,"E2"),sQuery(id+"F0.wireOp",EDGE,"E3"),sQuery(id+"F0.wireOp",EDGE,"E13.0"),sQuery(id+"F0.wireOp",EDGE,"E13.1"),sQuery(id+"F0.wireOp",EDGE,"E14.0"),subQ1,sQuery(id+"F0.wireOp",EDGE,"E15.1.1"),sQuery(id+"F0.wireOp",EDGE,"E15.1.2"),sQuery(id+"F0.wireOp",EDGE,"E15.1.5"),sQuery(id+"F0.wireOp",EDGE,"E15.1.6"),sQuery(id+"F0.wireOp",EDGE,"E15.1.7"),subQ0,sQuery(id+"F0.wireOp",EDGE,"E15.2.1"),sQuery(id+"F0.wireOp",EDGE,"E15.2.2"),sQuery(id+"F0.wireOp",EDGE,"E15.2.5"),sQuery(id+"F0.wireOp",EDGE,"E15.2.6"),sQuery(id+"F0.wireOp",EDGE,"E15.2.7"),sQuery(id+"F0.wireOp",EDGE,"E15.2.8")])],"isStart":true})]});}
            var Q12;
            {var subQ0=sQuery(id+"F0.wireOp",EDGE,"E14.0");var subQ1=sQuery(id+"F0.wireOp",EDGE,"E1");Q12=makeQuery(id+"F2.opFillet","BLEND_EDGE",EDGE,{"blendedFrom":[makeQuery(id+"F1.opExtrude","SWEPT_EDGE",EDGE,{"disambiguationData":[OSD([subQ1,subQ0])]}),makeQuery(id+"F1.opExtrude","CAP_FACE",FACE,{"disambiguationData":[OSD([subQ1,sQuery(id+"F0.wireOp",EDGE,"E2"),sQuery(id+"F0.wireOp",EDGE,"E3"),sQuery(id+"F0.wireOp",EDGE,"E13.0"),sQuery(id+"F0.wireOp",EDGE,"E13.1"),subQ0,sQuery(id+"F0.wireOp",EDGE,"E14.1"),sQuery(id+"F0.wireOp",EDGE,"E15.1.1"),sQuery(id+"F0.wireOp",EDGE,"E15.1.2"),sQuery(id+"F0.wireOp",EDGE,"E15.1.5"),sQuery(id+"F0.wireOp",EDGE,"E15.1.6"),sQuery(id+"F0.wireOp",EDGE,"E15.1.7"),sQuery(id+"F0.wireOp",EDGE,"E15.1.8"),sQuery(id+"F0.wireOp",EDGE,"E15.2.1"),sQuery(id+"F0.wireOp",EDGE,"E15.2.2"),sQuery(id+"F0.wireOp",EDGE,"E15.2.5"),sQuery(id+"F0.wireOp",EDGE,"E15.2.6"),sQuery(id+"F0.wireOp",EDGE,"E15.2.7"),sQuery(id+"F0.wireOp",EDGE,"E15.2.8")])],"isStart":true})],"blendedInto":[makeQuery(id+"F1.opExtrude","CAP_FACE",FACE,{"disambiguationData":[OSD([subQ1,sQuery(id+"F0.wireOp",EDGE,"E2"),sQuery(id+"F0.wireOp",EDGE,"E3"),sQuery(id+"F0.wireOp",EDGE,"E13.0"),sQuery(id+"F0.wireOp",EDGE,"E13.1"),subQ0,sQuery(id+"F0.wireOp",EDGE,"E14.1"),sQuery(id+"F0.wireOp",EDGE,"E15.1.1"),sQuery(id+"F0.wireOp",EDGE,"E15.1.2"),sQuery(id+"F0.wireOp",EDGE,"E15.1.5"),sQuery(id+"F0.wireOp",EDGE,"E15.1.6"),sQuery(id+"F0.wireOp",EDGE,"E15.1.7"),sQuery(id+"F0.wireOp",EDGE,"E15.1.8"),sQuery(id+"F0.wireOp",EDGE,"E15.2.1"),sQuery(id+"F0.wireOp",EDGE,"E15.2.2"),sQuery(id+"F0.wireOp",EDGE,"E15.2.5"),sQuery(id+"F0.wireOp",EDGE,"E15.2.6"),sQuery(id+"F0.wireOp",EDGE,"E15.2.7"),sQuery(id+"F0.wireOp",EDGE,"E15.2.8")])],"isStart":true})]});}
            var Q13;
            Q13=makeQuery(id+"F1.opExtrude","CAP_EDGE",EDGE,{"disambiguationData":[OSD([sQuery(id+"F0.wireOp",EDGE,"E1")])],"isStart":true});
            var Q14;
            {var subQ0=sQuery(id+"F0.wireOp",EDGE,"E13.0");var subQ1=sQuery(id+"F0.wireOp",EDGE,"E1");Q14=makeQuery(id+"F2.opFillet","BLEND_EDGE",EDGE,{"blendedFrom":[makeQuery(id+"F1.opExtrude","SWEPT_EDGE",EDGE,{"disambiguationData":[OSD([subQ1,subQ0])]}),makeQuery(id+"F1.opExtrude","CAP_FACE",FACE,{"disambiguationData":[OSD([subQ1,sQuery(id+"F0.wireOp",EDGE,"E2"),sQuery(id+"F0.wireOp",EDGE,"E3"),subQ0,sQuery(id+"F0.wireOp",EDGE,"E13.1"),sQuery(id+"F0.wireOp",EDGE,"E14.0"),sQuery(id+"F0.wireOp",EDGE,"E14.1"),sQuery(id+"F0.wireOp",EDGE,"E15.1.1"),sQuery(id+"F0.wireOp",EDGE,"E15.1.2"),sQuery(id+"F0.wireOp",EDGE,"E15.1.5"),sQuery(id+"F0.wireOp",EDGE,"E15.1.6"),sQuery(id+"F0.wireOp",EDGE,"E15.1.7"),sQuery(id+"F0.wireOp",EDGE,"E15.1.8"),sQuery(id+"F0.wireOp",EDGE,"E15.2.1"),sQuery(id+"F0.wireOp",EDGE,"E15.2.2"),sQuery(id+"F0.wireOp",EDGE,"E15.2.5"),sQuery(id+"F0.wireOp",EDGE,"E15.2.6"),sQuery(id+"F0.wireOp",EDGE,"E15.2.7"),sQuery(id+"F0.wireOp",EDGE,"E15.2.8")])],"isStart":true})],"blendedInto":[makeQuery(id+"F1.opExtrude","CAP_FACE",FACE,{"disambiguationData":[OSD([subQ1,sQuery(id+"F0.wireOp",EDGE,"E2"),sQuery(id+"F0.wireOp",EDGE,"E3"),subQ0,sQuery(id+"F0.wireOp",EDGE,"E13.1"),sQuery(id+"F0.wireOp",EDGE,"E14.0"),sQuery(id+"F0.wireOp",EDGE,"E14.1"),sQuery(id+"F0.wireOp",EDGE,"E15.1.1"),sQuery(id+"F0.wireOp",EDGE,"E15.1.2"),sQuery(id+"F0.wireOp",EDGE,"E15.1.5"),sQuery(id+"F0.wireOp",EDGE,"E15.1.6"),sQuery(id+"F0.wireOp",EDGE,"E15.1.7"),sQuery(id+"F0.wireOp",EDGE,"E15.1.8"),sQuery(id+"F0.wireOp",EDGE,"E15.2.1"),sQuery(id+"F0.wireOp",EDGE,"E15.2.2"),sQuery(id+"F0.wireOp",EDGE,"E15.2.5"),sQuery(id+"F0.wireOp",EDGE,"E15.2.6"),sQuery(id+"F0.wireOp",EDGE,"E15.2.7"),sQuery(id+"F0.wireOp",EDGE,"E15.2.8")])],"isStart":true})]});}
            var Q15;
            {var subQ0=sQuery(id+"F0.wireOp",EDGE,"E15.2.7");var subQ1=sQuery(id+"F0.wireOp",EDGE,"E13.1");Q15=makeQuery(id+"F3.opFillet","BLEND_EDGE",EDGE,{"blendedFrom":[makeQuery(id+"F1.opExtrude","SWEPT_EDGE",EDGE,{"disambiguationData":[OSD([subQ1,subQ0])]}),makeQuery(id+"F1.opExtrude","CAP_FACE",FACE,{"disambiguationData":[OSD([sQuery(id+"F0.wireOp",EDGE,"E1"),sQuery(id+"F0.wireOp",EDGE,"E2"),sQuery(id+"F0.wireOp",EDGE,"E3"),sQuery(id+"F0.wireOp",EDGE,"E13.0"),subQ1,sQuery(id+"F0.wireOp",EDGE,"E14.0"),sQuery(id+"F0.wireOp",EDGE,"E14.1"),sQuery(id+"F0.wireOp",EDGE,"E15.1.1"),sQuery(id+"F0.wireOp",EDGE,"E15.1.2"),sQuery(id+"F0.wireOp",EDGE,"E15.1.5"),sQuery(id+"F0.wireOp",EDGE,"E15.1.6"),sQuery(id+"F0.wireOp",EDGE,"E15.1.7"),sQuery(id+"F0.wireOp",EDGE,"E15.1.8"),sQuery(id+"F0.wireOp",EDGE,"E15.2.1"),sQuery(id+"F0.wireOp",EDGE,"E15.2.2"),sQuery(id+"F0.wireOp",EDGE,"E15.2.5"),sQuery(id+"F0.wireOp",EDGE,"E15.2.6"),subQ0,sQuery(id+"F0.wireOp",EDGE,"E15.2.8")])],"isStart":true})],"blendedInto":[makeQuery(id+"F1.opExtrude","CAP_FACE",FACE,{"disambiguationData":[OSD([sQuery(id+"F0.wireOp",EDGE,"E1"),sQuery(id+"F0.wireOp",EDGE,"E2"),sQuery(id+"F0.wireOp",EDGE,"E3"),sQuery(id+"F0.wireOp",EDGE,"E13.0"),subQ1,sQuery(id+"F0.wireOp",EDGE,"E14.0"),sQuery(id+"F0.wireOp",EDGE,"E14.1"),sQuery(id+"F0.wireOp",EDGE,"E15.1.1"),sQuery(id+"F0.wireOp",EDGE,"E15.1.2"),sQuery(id+"F0.wireOp",EDGE,"E15.1.5"),sQuery(id+"F0.wireOp",EDGE,"E15.1.6"),sQuery(id+"F0.wireOp",EDGE,"E15.1.7"),sQuery(id+"F0.wireOp",EDGE,"E15.1.8"),sQuery(id+"F0.wireOp",EDGE,"E15.2.1"),sQuery(id+"F0.wireOp",EDGE,"E15.2.2"),sQuery(id+"F0.wireOp",EDGE,"E15.2.5"),sQuery(id+"F0.wireOp",EDGE,"E15.2.6"),subQ0,sQuery(id+"F0.wireOp",EDGE,"E15.2.8")])],"isStart":true})]});}
            var Q16;
            Q16=makeQuery(id+"F1.opExtrude","CAP_EDGE",EDGE,{"disambiguationData":[OSD([sQuery(id+"F0.wireOp",EDGE,"E15.2.6")])],"isStart":true});
            var Q17;
            {var subQ0=sQuery(id+"F0.wireOp",EDGE,"E15.2.6");var subQ1=sQuery(id+"F0.wireOp",EDGE,"E15.2.1");Q17=makeQuery(id+"F2.opFillet","BLEND_EDGE",EDGE,{"blendedFrom":[makeQuery(id+"F1.opExtrude","SWEPT_EDGE",EDGE,{"disambiguationData":[OSD([subQ1,subQ0])]}),makeQuery(id+"F1.opExtrude","CAP_FACE",FACE,{"disambiguationData":[OSD([sQuery(id+"F0.wireOp",EDGE,"E1"),sQuery(id+"F0.wireOp",EDGE,"E2"),sQuery(id+"F0.wireOp",EDGE,"E3"),sQuery(id+"F0.wireOp",EDGE,"E13.0"),sQuery(id+"F0.wireOp",EDGE,"E13.1"),sQuery(id+"F0.wireOp",EDGE,"E14.0"),sQuery(id+"F0.wireOp",EDGE,"E14.1"),sQuery(id+"F0.wireOp",EDGE,"E15.1.1"),sQuery(id+"F0.wireOp",EDGE,"E15.1.2"),sQuery(id+"F0.wireOp",EDGE,"E15.1.5"),sQuery(id+"F0.wireOp",EDGE,"E15.1.6"),sQuery(id+"F0.wireOp",EDGE,"E15.1.7"),sQuery(id+"F0.wireOp",EDGE,"E15.1.8"),subQ1,sQuery(id+"F0.wireOp",EDGE,"E15.2.2"),sQuery(id+"F0.wireOp",EDGE,"E15.2.5"),subQ0,sQuery(id+"F0.wireOp",EDGE,"E15.2.7"),sQuery(id+"F0.wireOp",EDGE,"E15.2.8")])],"isStart":true})],"blendedInto":[makeQuery(id+"F1.opExtrude","CAP_FACE",FACE,{"disambiguationData":[OSD([sQuery(id+"F0.wireOp",EDGE,"E1"),sQuery(id+"F0.wireOp",EDGE,"E2"),sQuery(id+"F0.wireOp",EDGE,"E3"),sQuery(id+"F0.wireOp",EDGE,"E13.0"),sQuery(id+"F0.wireOp",EDGE,"E13.1"),sQuery(id+"F0.wireOp",EDGE,"E14.0"),sQuery(id+"F0.wireOp",EDGE,"E14.1"),sQuery(id+"F0.wireOp",EDGE,"E15.1.1"),sQuery(id+"F0.wireOp",EDGE,"E15.1.2"),sQuery(id+"F0.wireOp",EDGE,"E15.1.5"),sQuery(id+"F0.wireOp",EDGE,"E15.1.6"),sQuery(id+"F0.wireOp",EDGE,"E15.1.7"),sQuery(id+"F0.wireOp",EDGE,"E15.1.8"),subQ1,sQuery(id+"F0.wireOp",EDGE,"E15.2.2"),sQuery(id+"F0.wireOp",EDGE,"E15.2.5"),subQ0,sQuery(id+"F0.wireOp",EDGE,"E15.2.7"),sQuery(id+"F0.wireOp",EDGE,"E15.2.8")])],"isStart":true})]});}
            var Q18;
            {var subQ0=sQuery(id+"F0.wireOp",EDGE,"E15.2.6");var subQ1=sQuery(id+"F0.wireOp",EDGE,"E15.2.2");Q18=makeQuery(id+"F2.opFillet","BLEND_EDGE",EDGE,{"blendedFrom":[makeQuery(id+"F1.opExtrude","SWEPT_EDGE",EDGE,{"disambiguationData":[OSD([subQ1,subQ0])]}),makeQuery(id+"F1.opExtrude","CAP_FACE",FACE,{"disambiguationData":[OSD([sQuery(id+"F0.wireOp",EDGE,"E1"),sQuery(id+"F0.wireOp",EDGE,"E2"),sQuery(id+"F0.wireOp",EDGE,"E3"),sQuery(id+"F0.wireOp",EDGE,"E13.0"),sQuery(id+"F0.wireOp",EDGE,"E13.1"),sQuery(id+"F0.wireOp",EDGE,"E14.0"),sQuery(id+"F0.wireOp",EDGE,"E14.1"),sQuery(id+"F0.wireOp",EDGE,"E15.1.1"),sQuery(id+"F0.wireOp",EDGE,"E15.1.2"),sQuery(id+"F0.wireOp",EDGE,"E15.1.5"),sQuery(id+"F0.wireOp",EDGE,"E15.1.6"),sQuery(id+"F0.wireOp",EDGE,"E15.1.7"),sQuery(id+"F0.wireOp",EDGE,"E15.1.8"),sQuery(id+"F0.wireOp",EDGE,"E15.2.1"),subQ1,sQuery(id+"F0.wireOp",EDGE,"E15.2.5"),subQ0,sQuery(id+"F0.wireOp",EDGE,"E15.2.7"),sQuery(id+"F0.wireOp",EDGE,"E15.2.8")])],"isStart":true})],"blendedInto":[makeQuery(id+"F1.opExtrude","CAP_FACE",FACE,{"disambiguationData":[OSD([sQuery(id+"F0.wireOp",EDGE,"E1"),sQuery(id+"F0.wireOp",EDGE,"E2"),sQuery(id+"F0.wireOp",EDGE,"E3"),sQuery(id+"F0.wireOp",EDGE,"E13.0"),sQuery(id+"F0.wireOp",EDGE,"E13.1"),sQuery(id+"F0.wireOp",EDGE,"E14.0"),sQuery(id+"F0.wireOp",EDGE,"E14.1"),sQuery(id+"F0.wireOp",EDGE,"E15.1.1"),sQuery(id+"F0.wireOp",EDGE,"E15.1.2"),sQuery(id+"F0.wireOp",EDGE,"E15.1.5"),sQuery(id+"F0.wireOp",EDGE,"E15.1.6"),sQuery(id+"F0.wireOp",EDGE,"E15.1.7"),sQuery(id+"F0.wireOp",EDGE,"E15.1.8"),sQuery(id+"F0.wireOp",EDGE,"E15.2.1"),subQ1,sQuery(id+"F0.wireOp",EDGE,"E15.2.5"),subQ0,sQuery(id+"F0.wireOp",EDGE,"E15.2.7"),sQuery(id+"F0.wireOp",EDGE,"E15.2.8")])],"isStart":true})]});}
            var Q19;
            {var subQ0=sQuery(id+"F0.wireOp",EDGE,"E15.2.8");var subQ1=sQuery(id+"F0.wireOp",EDGE,"E15.1.7");Q19=makeQuery(id+"F3.opFillet","BLEND_EDGE",EDGE,{"blendedFrom":[makeQuery(id+"F1.opExtrude","SWEPT_EDGE",EDGE,{"disambiguationData":[OSD([sQuery(id+"F0.wireOp",EDGE,"E6"),subQ1,subQ0])]}),makeQuery(id+"F1.opExtrude","CAP_FACE",FACE,{"disambiguationData":[OSD([sQuery(id+"F0.wireOp",EDGE,"E1"),sQuery(id+"F0.wireOp",EDGE,"E2"),sQuery(id+"F0.wireOp",EDGE,"E3"),sQuery(id+"F0.wireOp",EDGE,"E13.0"),sQuery(id+"F0.wireOp",EDGE,"E13.1"),sQuery(id+"F0.wireOp",EDGE,"E14.0"),sQuery(id+"F0.wireOp",EDGE,"E14.1"),sQuery(id+"F0.wireOp",EDGE,"E15.1.1"),sQuery(id+"F0.wireOp",EDGE,"E15.1.2"),sQuery(id+"F0.wireOp",EDGE,"E15.1.5"),sQuery(id+"F0.wireOp",EDGE,"E15.1.6"),subQ1,sQuery(id+"F0.wireOp",EDGE,"E15.1.8"),sQuery(id+"F0.wireOp",EDGE,"E15.2.1"),sQuery(id+"F0.wireOp",EDGE,"E15.2.2"),sQuery(id+"F0.wireOp",EDGE,"E15.2.5"),sQuery(id+"F0.wireOp",EDGE,"E15.2.6"),sQuery(id+"F0.wireOp",EDGE,"E15.2.7"),subQ0])],"isStart":true})],"blendedInto":[makeQuery(id+"F1.opExtrude","CAP_FACE",FACE,{"disambiguationData":[OSD([sQuery(id+"F0.wireOp",EDGE,"E1"),sQuery(id+"F0.wireOp",EDGE,"E2"),sQuery(id+"F0.wireOp",EDGE,"E3"),sQuery(id+"F0.wireOp",EDGE,"E13.0"),sQuery(id+"F0.wireOp",EDGE,"E13.1"),sQuery(id+"F0.wireOp",EDGE,"E14.0"),sQuery(id+"F0.wireOp",EDGE,"E14.1"),sQuery(id+"F0.wireOp",EDGE,"E15.1.1"),sQuery(id+"F0.wireOp",EDGE,"E15.1.2"),sQuery(id+"F0.wireOp",EDGE,"E15.1.5"),sQuery(id+"F0.wireOp",EDGE,"E15.1.6"),subQ1,sQuery(id+"F0.wireOp",EDGE,"E15.1.8"),sQuery(id+"F0.wireOp",EDGE,"E15.2.1"),sQuery(id+"F0.wireOp",EDGE,"E15.2.2"),sQuery(id+"F0.wireOp",EDGE,"E15.2.5"),sQuery(id+"F0.wireOp",EDGE,"E15.2.6"),sQuery(id+"F0.wireOp",EDGE,"E15.2.7"),subQ0])],"isStart":true})]});}
            var Q20;
            Q20=makeQuery(id+"F1.opExtrude","CAP_EDGE",EDGE,{"disambiguationData":[OSD([sQuery(id+"F0.wireOp",EDGE,"E15.1.6")])],"isStart":true});
            var Q21;
            {var subQ0=sQuery(id+"F0.wireOp",EDGE,"E15.1.6");var subQ1=sQuery(id+"F0.wireOp",EDGE,"E15.1.1");Q21=makeQuery(id+"F2.opFillet","BLEND_EDGE",EDGE,{"blendedFrom":[makeQuery(id+"F1.opExtrude","SWEPT_EDGE",EDGE,{"disambiguationData":[OSD([subQ1,subQ0])]}),makeQuery(id+"F1.opExtrude","CAP_FACE",FACE,{"disambiguationData":[OSD([sQuery(id+"F0.wireOp",EDGE,"E1"),sQuery(id+"F0.wireOp",EDGE,"E2"),sQuery(id+"F0.wireOp",EDGE,"E3"),sQuery(id+"F0.wireOp",EDGE,"E13.0"),sQuery(id+"F0.wireOp",EDGE,"E13.1"),sQuery(id+"F0.wireOp",EDGE,"E14.0"),sQuery(id+"F0.wireOp",EDGE,"E14.1"),subQ1,sQuery(id+"F0.wireOp",EDGE,"E15.1.2"),sQuery(id+"F0.wireOp",EDGE,"E15.1.5"),subQ0,sQuery(id+"F0.wireOp",EDGE,"E15.1.7"),sQuery(id+"F0.wireOp",EDGE,"E15.1.8"),sQuery(id+"F0.wireOp",EDGE,"E15.2.1"),sQuery(id+"F0.wireOp",EDGE,"E15.2.2"),sQuery(id+"F0.wireOp",EDGE,"E15.2.5"),sQuery(id+"F0.wireOp",EDGE,"E15.2.6"),sQuery(id+"F0.wireOp",EDGE,"E15.2.7"),sQuery(id+"F0.wireOp",EDGE,"E15.2.8")])],"isStart":true})],"blendedInto":[makeQuery(id+"F1.opExtrude","CAP_FACE",FACE,{"disambiguationData":[OSD([sQuery(id+"F0.wireOp",EDGE,"E1"),sQuery(id+"F0.wireOp",EDGE,"E2"),sQuery(id+"F0.wireOp",EDGE,"E3"),sQuery(id+"F0.wireOp",EDGE,"E13.0"),sQuery(id+"F0.wireOp",EDGE,"E13.1"),sQuery(id+"F0.wireOp",EDGE,"E14.0"),sQuery(id+"F0.wireOp",EDGE,"E14.1"),subQ1,sQuery(id+"F0.wireOp",EDGE,"E15.1.2"),sQuery(id+"F0.wireOp",EDGE,"E15.1.5"),subQ0,sQuery(id+"F0.wireOp",EDGE,"E15.1.7"),sQuery(id+"F0.wireOp",EDGE,"E15.1.8"),sQuery(id+"F0.wireOp",EDGE,"E15.2.1"),sQuery(id+"F0.wireOp",EDGE,"E15.2.2"),sQuery(id+"F0.wireOp",EDGE,"E15.2.5"),sQuery(id+"F0.wireOp",EDGE,"E15.2.6"),sQuery(id+"F0.wireOp",EDGE,"E15.2.7"),sQuery(id+"F0.wireOp",EDGE,"E15.2.8")])],"isStart":true})]});}
            var Q22;
            {var subQ0=sQuery(id+"F0.wireOp",EDGE,"E15.1.6");var subQ1=sQuery(id+"F0.wireOp",EDGE,"E15.1.2");Q22=makeQuery(id+"F2.opFillet","BLEND_EDGE",EDGE,{"blendedFrom":[makeQuery(id+"F1.opExtrude","SWEPT_EDGE",EDGE,{"disambiguationData":[OSD([subQ1,subQ0])]}),makeQuery(id+"F1.opExtrude","CAP_FACE",FACE,{"disambiguationData":[OSD([sQuery(id+"F0.wireOp",EDGE,"E1"),sQuery(id+"F0.wireOp",EDGE,"E2"),sQuery(id+"F0.wireOp",EDGE,"E3"),sQuery(id+"F0.wireOp",EDGE,"E13.0"),sQuery(id+"F0.wireOp",EDGE,"E13.1"),sQuery(id+"F0.wireOp",EDGE,"E14.0"),sQuery(id+"F0.wireOp",EDGE,"E14.1"),sQuery(id+"F0.wireOp",EDGE,"E15.1.1"),subQ1,sQuery(id+"F0.wireOp",EDGE,"E15.1.5"),subQ0,sQuery(id+"F0.wireOp",EDGE,"E15.1.7"),sQuery(id+"F0.wireOp",EDGE,"E15.1.8"),sQuery(id+"F0.wireOp",EDGE,"E15.2.1"),sQuery(id+"F0.wireOp",EDGE,"E15.2.2"),sQuery(id+"F0.wireOp",EDGE,"E15.2.5"),sQuery(id+"F0.wireOp",EDGE,"E15.2.6"),sQuery(id+"F0.wireOp",EDGE,"E15.2.7"),sQuery(id+"F0.wireOp",EDGE,"E15.2.8")])],"isStart":true})],"blendedInto":[makeQuery(id+"F1.opExtrude","CAP_FACE",FACE,{"disambiguationData":[OSD([sQuery(id+"F0.wireOp",EDGE,"E1"),sQuery(id+"F0.wireOp",EDGE,"E2"),sQuery(id+"F0.wireOp",EDGE,"E3"),sQuery(id+"F0.wireOp",EDGE,"E13.0"),sQuery(id+"F0.wireOp",EDGE,"E13.1"),sQuery(id+"F0.wireOp",EDGE,"E14.0"),sQuery(id+"F0.wireOp",EDGE,"E14.1"),sQuery(id+"F0.wireOp",EDGE,"E15.1.1"),subQ1,sQuery(id+"F0.wireOp",EDGE,"E15.1.5"),subQ0,sQuery(id+"F0.wireOp",EDGE,"E15.1.7"),sQuery(id+"F0.wireOp",EDGE,"E15.1.8"),sQuery(id+"F0.wireOp",EDGE,"E15.2.1"),sQuery(id+"F0.wireOp",EDGE,"E15.2.2"),sQuery(id+"F0.wireOp",EDGE,"E15.2.5"),sQuery(id+"F0.wireOp",EDGE,"E15.2.6"),sQuery(id+"F0.wireOp",EDGE,"E15.2.7"),sQuery(id+"F0.wireOp",EDGE,"E15.2.8")])],"isStart":true})]});}
            fillet(context, id + "F5", {"entities" : qUnion([Q0, Q1, Q2, Q3, Q4, Q5, Q6, Q7, Q8, Q9, Q10, Q11, Q12, Q13, Q14, Q15, Q16, Q17, Q18, Q19, Q20, Q21, Q22]), "radius" : 2.54 * mm, "tangentPropagation" : true, "allowEdgeOverflow" : false});
        }
    });
